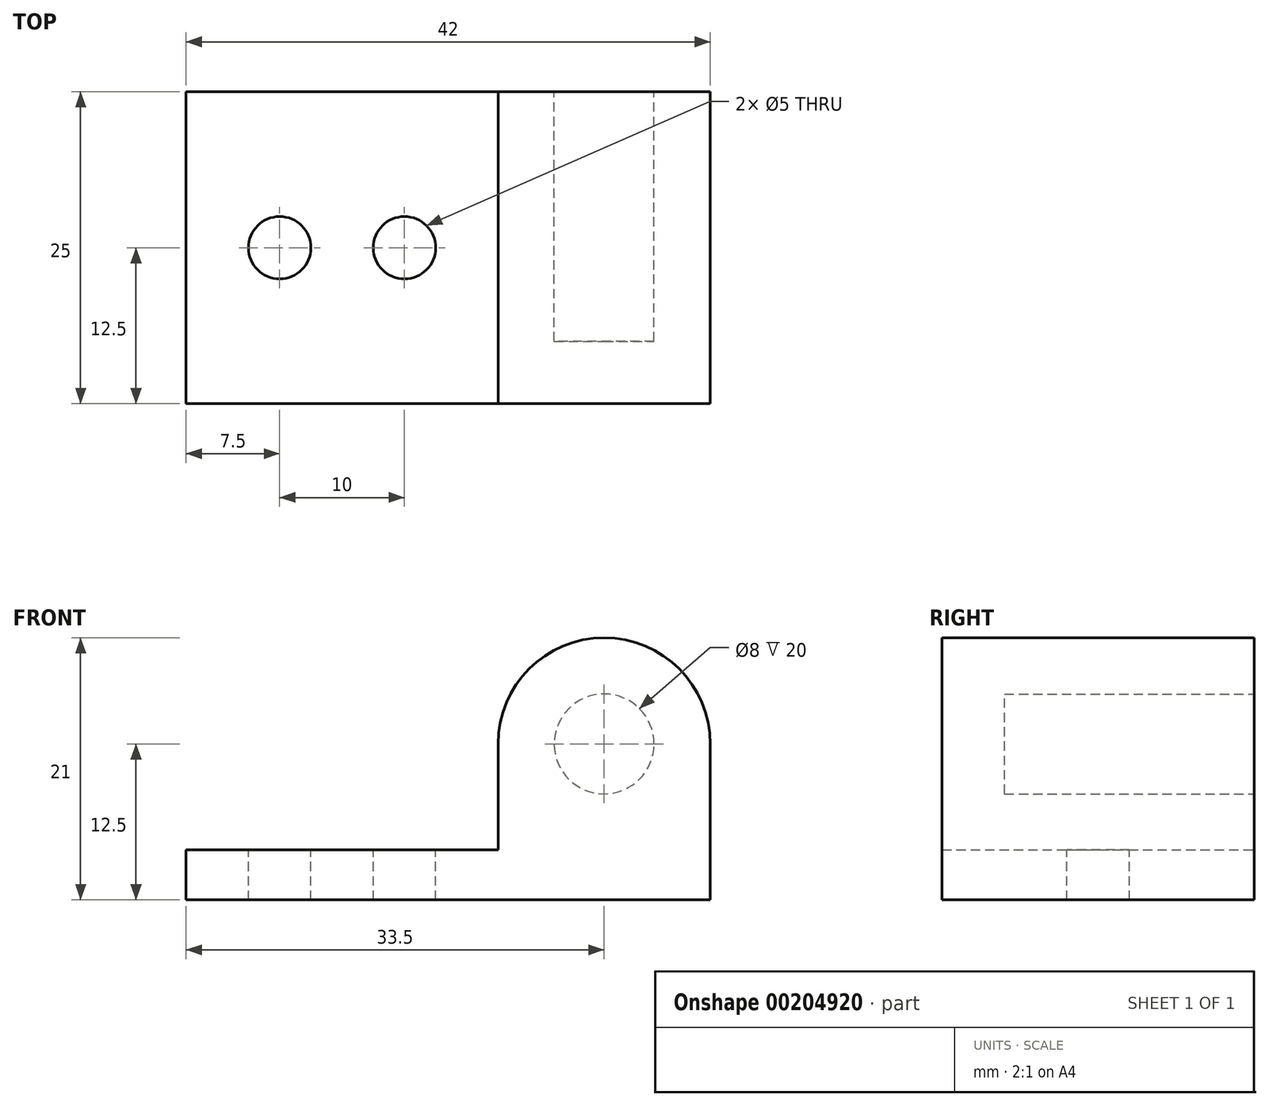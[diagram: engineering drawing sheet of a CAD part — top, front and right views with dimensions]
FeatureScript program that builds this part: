
annotation { "Feature Type Name" : "Feature", "Feature Type Description" : "" }
export const myFeature = defineFeature(function(context is Context, id is Id, definition is map)
    precondition{}
    {
        {
            var Q0;
            Q0=qCreatedBy(makeId("Front.planeOp"),FACE);
            var sketch = newSketch(context, id + "F0", { "sketchPlane" : qUnion([Q0])});
            skLineSegment(sketch, "E0", {"start": v(0, 0) * mm, "end": v(42, 0) * mm});
            skLineSegment(sketch, "E1", {"start": v(42, 0) * mm, "end": v(42, 4) * mm});
            skLineSegment(sketch, "E2", {"start": v(42, 4) * mm, "end": v(0, 4) * mm});
            skLineSegment(sketch, "E3", {"start": v(0, 4) * mm, "end": v(0, 0) * mm});
            skCircle(sketch, "E4", {"center": v(33.5, 12.5) * mm, "radius": 4 * mm});
            skCircle(sketch, "E5", {"center": v(33.5, 12.5) * mm, "radius": 8.5 * mm});
            skLineSegment(sketch, "E6", {"start": v(42, 4) * mm, "end": v(42, 21.37) * mm});
            skLineSegment(sketch, "E7", {"start": v(33.5, 12.5) * mm, "end": v(25, 12.5) * mm});
            skLineSegment(sketch, "E8", {"start": v(25, 12.5) * mm, "end": v(25, 4) * mm});
            skSolve(sketch);
        }
        {
            var Q0;
            Q0=makeQuery(id+"F0.imprint","IMPRINT",FACE,{"disambiguationData":[TD([[makeQuery(id+"F0.imprint","IMPRINT",EDGE,{"derivedFrom":sQuery(id+"F0.wireOp",EDGE,"E0")}),1.0]])]});
            var Q1;
            {var subQ3=sQuery(id+"F0.wireOp",EDGE,"E8");Q1=makeQuery(id+"F0.imprint","IMPRINT",FACE,{"disambiguationData":[TD([[makeQuery(id+"F0.imprint","IMPRINT",EDGE,{"derivedFrom":subQ3}),1.0]])]});}
            var Q2;
            Q2=makeQuery(id+"F0.imprint","IMPRINT",FACE,{"disambiguationData":[TD([[makeQuery(id+"F0.imprint","IMPRINT",EDGE,{"derivedFrom":sQuery(id+"F0.wireOp",EDGE,"E4")}),-1.0]])]});
            var Q3;
            {var subQ0=sQuery(id+"F0.wireOp",EDGE,"E6");var subQ3=sQuery(id+"F0.wireOp",EDGE,"E5");var subQ5=makeQuery(id+"F0.imprint","INTERSECT",VERTEX,{"derivedFrom":[subQ3,subQ0]});Q3=makeQuery(id+"F0.imprint","IMPRINT",FACE,{"disambiguationData":[TD([[makeQuery(id+"F0.imprint","IMPRINT",EDGE,{"disambiguationData":[TD([[subQ5,1.0]])],"derivedFrom":subQ3}),-1.0]])]});}
            extrude(context, id + "F1", {"entities" : qUnion([Q0, Q1, Q2, Q3]), "depth" : 25 * mm});
        }
        {
            var Q0;
            Q0=makeQuery(id+"F1.opExtrude","SWEPT_FACE",FACE,{"disambiguationData":[OSD([sQuery(id+"F0.wireOp",EDGE,"E2")])]});
            var sketch = newSketch(context, id + "F2", { "sketchPlane" : qUnion([Q0])});
            skLineSegment(sketch, "E9", {"start": v(0, -12.5) * mm, "end": v(25, -12.5) * mm});
            skCircle(sketch, "E10", {"center": v(7.5, -12.5) * mm, "radius": 2.5 * mm});
            skCircle(sketch, "E11", {"center": v(17.5, -12.5) * mm, "radius": 2.5 * mm});
            skSolve(sketch);
        }
        {
            var Q0;
            {var subQ0=sQuery(id+"F2.wireOp",EDGE,"E10");var subQ1=sQuery(id+"F2.wireOp",EDGE,"E9");var subQ2=makeQuery(id+"F2.imprint","INTERSECT",VERTEX,{"disambiguationData":[OD(0.0)],"derivedFrom":[subQ1,subQ0]});Q0=makeQuery(id+"F2.imprint","IMPRINT",FACE,{"disambiguationData":[TD([[makeQuery(id+"F2.imprint","IMPRINT",EDGE,{"disambiguationData":[TD([[subQ2,-1.0]])],"derivedFrom":subQ1}),-1.0]])]});}
            var Q1;
            {var subQ0=sQuery(id+"F2.wireOp",EDGE,"E10");var subQ1=sQuery(id+"F2.wireOp",EDGE,"E9");var subQ2=makeQuery(id+"F2.imprint","INTERSECT",VERTEX,{"disambiguationData":[OD(0.0)],"derivedFrom":[subQ1,subQ0]});Q1=makeQuery(id+"F2.imprint","IMPRINT",FACE,{"disambiguationData":[TD([[makeQuery(id+"F2.imprint","IMPRINT",EDGE,{"disambiguationData":[TD([[subQ2,-1.0]])],"derivedFrom":subQ1}),1.0]])]});}
            var Q2;
            {var subQ0=sQuery(id+"F2.wireOp",EDGE,"E11");var subQ1=sQuery(id+"F2.wireOp",EDGE,"E9");var subQ2=makeQuery(id+"F2.imprint","INTERSECT",VERTEX,{"disambiguationData":[OD(0.0)],"derivedFrom":[subQ1,subQ0]});Q2=makeQuery(id+"F2.imprint","IMPRINT",FACE,{"disambiguationData":[TD([[makeQuery(id+"F2.imprint","IMPRINT",EDGE,{"disambiguationData":[TD([[subQ2,-1.0]])],"derivedFrom":subQ1}),-1.0]])]});}
            var Q3;
            {var subQ0=sQuery(id+"F2.wireOp",EDGE,"E11");var subQ1=sQuery(id+"F2.wireOp",EDGE,"E9");var subQ2=makeQuery(id+"F2.imprint","INTERSECT",VERTEX,{"disambiguationData":[OD(0.0)],"derivedFrom":[subQ1,subQ0]});Q3=makeQuery(id+"F2.imprint","IMPRINT",FACE,{"disambiguationData":[TD([[makeQuery(id+"F2.imprint","IMPRINT",EDGE,{"disambiguationData":[TD([[subQ2,-1.0]])],"derivedFrom":subQ1}),1.0]])]});}
            extrude(context, id + "F3", {"entities" : qUnion([Q0, Q1, Q2, Q3]), "operationType" : NewBodyOperationType.REMOVE, "oppositeDirection" : true, "depth" : 25 * mm});
        }
        {
            var Q0;
            Q0=makeQuery(id+"F1.opExtrude","CAP_FACE",FACE,{"disambiguationData":[OSD([sQuery(id+"F0.wireOp",EDGE,"E0"),sQuery(id+"F0.wireOp",EDGE,"E1"),sQuery(id+"F0.wireOp",EDGE,"E2"),sQuery(id+"F0.wireOp",EDGE,"E3"),sQuery(id+"F0.wireOp",EDGE,"E4"),sQuery(id+"F0.wireOp",EDGE,"E5"),sQuery(id+"F0.wireOp",EDGE,"E6"),sQuery(id+"F0.wireOp",EDGE,"E8")])],"isStart":false});
            var sketch = newSketch(context, id + "F4", { "sketchPlane" : qUnion([Q0])});
            skCircle(sketch, "E12", {"center": v(33.5, 12.5) * mm, "radius": 4 * mm});
            skSolve(sketch);
        }
        {
            var Q0;
            Q0=makeQuery(id+"F4.imprint","IMPRINT",FACE,{"disambiguationData":[TD([[makeQuery(id+"F4.imprint","IMPRINT",EDGE,{"derivedFrom":sQuery(id+"F4.wireOp",EDGE,"E12")}),1.0]])]});
            extrude(context, id + "F5", {"entities" : qUnion([Q0]), "operationType" : NewBodyOperationType.ADD, "oppositeDirection" : true, "depth" : 5 * mm});
        }
    });
